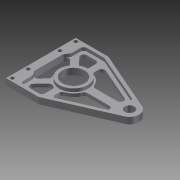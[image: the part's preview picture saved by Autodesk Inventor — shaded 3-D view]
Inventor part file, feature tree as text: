
AUTODESK INVENTOR PART (.ipt)
format: ipt  version: 2012 (Build 160160000, 160)  size: 278,016 bytes
history: native  units: in
note: dims shown in document units (in); Inventor stores cm internally (conversion verified against a paired STEP export)
features: extrude x3, fillet x3, sketch x2, hole x1
ambient origin geometry x8: Origin, YZ Plane, XZ Plane, XY Plane, X Axis, Y Axis, Z Axis, Center Point
bodies: Solid1 (feature_tree)
feature tree (9):
  sketch  "Sketch1"  dims[d0=2.75in d1=3.5in]
  extrude  "Extrusion1"  Depth=3.5in
  extrude  "Extrusion2"  Depth=0.1621in
  fillet  "Fillet1"  Radius=0.375in
  hole  "Hole1"  [1 undecoded]
  sketch  "Sketch2"  dims[d2=1.375in d6=0.1621in d7=0.375in d8=1.289in d9=0.875in d10=0.125in d11=0.0in d12=0.625in d13=0.1562in d14=0.1562in d15=0.25in d16=0.25in d17=0.125in d18=0.125in d19=0.125in d20=0.125in d21=0.125in d22=0.125in d24=0.125in d25=0.125in d26=0.25in d27=0.3125in d28=0.25in d29=0.125in d30=0.0in d31=0.125in d32=0.125in d33=0.125in d35=0.125in d36=0.125in d38=0.144in d39=0.75in d40=0.25in d41=0.25in d42=0.5635in d43=1.0in d44=0.8108in d45=0.4375in d46=0.125in d47=0.125in d48=0.125in d49=0.125in d51=0.125in d53=0.875in d54=0.0625in d58=0.125in d59=0.0in d62=0.75in d63=0.75in d69=0.125in d70=0.1621in d71=0.375in d72=1.125in d73=0.125in d74=0.25in]
  extrude  "Extrusion4"  Depth=0.875in
  fillet  "Fillet6"  Radius=0.125in
  fillet  "Fillet7"  Radius=0.625in
note: 1 required parameter value undecoded (feature->parameter linkage not recoverable at this tier; creation-order binding heuristic only, values carry confidence <= 0.55)
